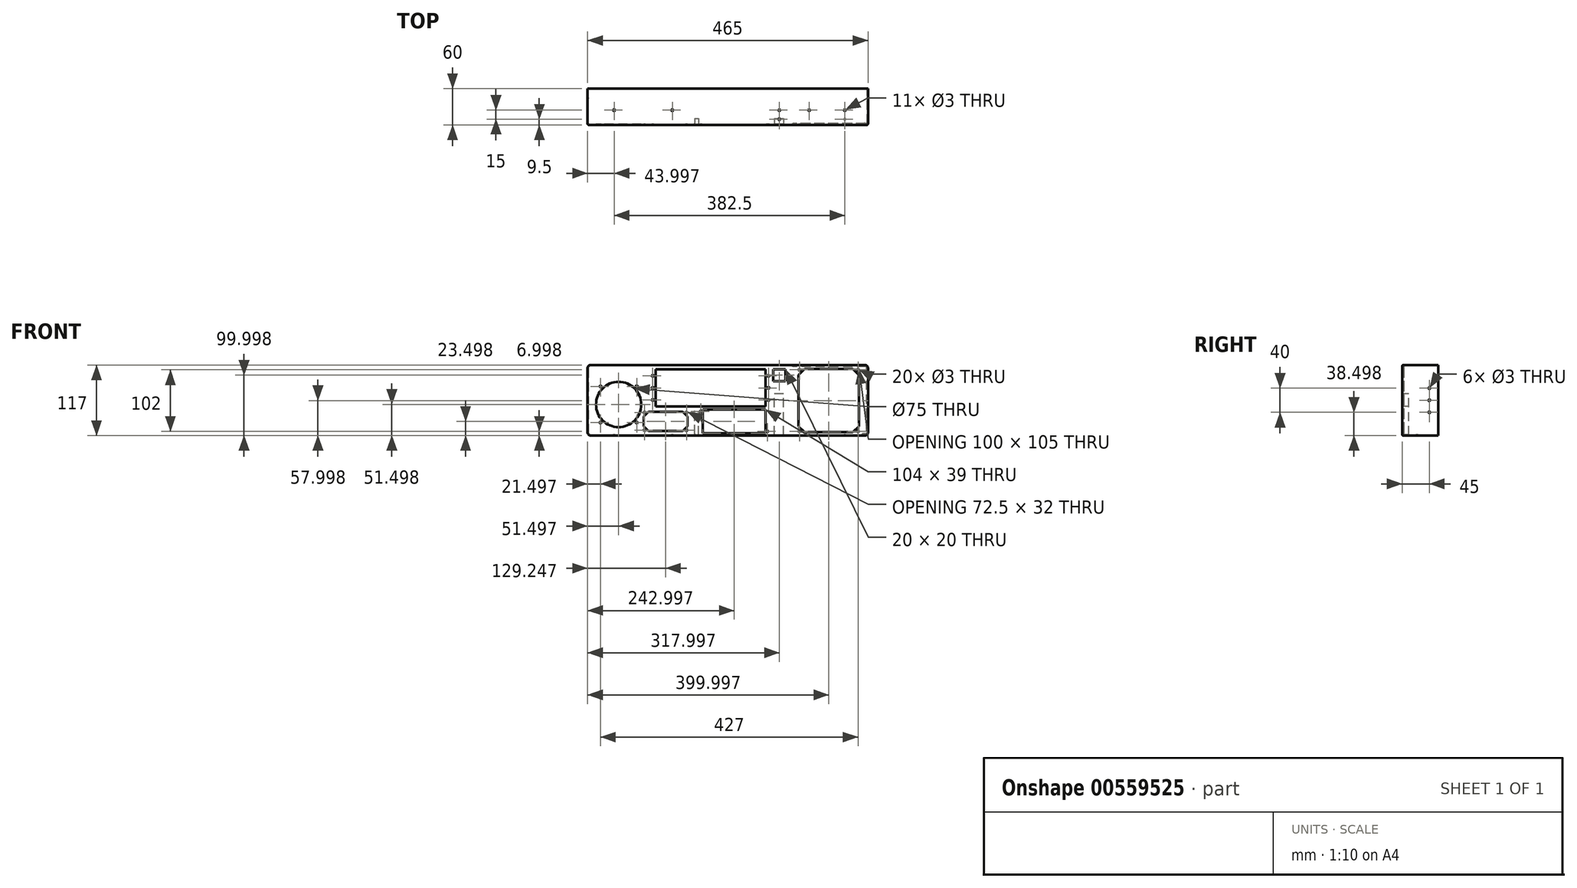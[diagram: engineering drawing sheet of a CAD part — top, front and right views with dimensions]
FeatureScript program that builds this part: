
annotation { "Feature Type Name" : "Feature", "Feature Type Description" : "" }
export const myFeature = defineFeature(function(context is Context, id is Id, definition is map)
    precondition{}
    {
        {
            var Q0;
            Q0=qCreatedBy(makeId("Front.planeOp"),FACE);
            var sketch = newSketch(context, id + "F0", { "sketchPlane" : qUnion([Q0])});
            skLineSegment(sketch, "E0.bottom", {"start": v(-245.15, 85.69) * mm, "end": v(219.85, 85.69) * mm});
            skLineSegment(sketch, "E0.top", {"start": v(-245.15, -31.31) * mm, "end": v(219.85, -31.31) * mm});
            skLineSegment(sketch, "E0.left", {"start": v(-245.15, 85.69) * mm, "end": v(-245.15, -31.31) * mm});
            skLineSegment(sketch, "E0.right", {"start": v(219.85, 85.69) * mm, "end": v(219.85, -31.31) * mm});
            skSolve(sketch);
        }
        {
            var Q0;
            Q0=qSketchRegion(id+"F0",true);
            var Q1;
            Q1=makeQuery(id+"F0.imprint","IMPRINT",FACE,{"disambiguationData":[TD([[makeQuery(id+"F0.imprint","IMPRINT",EDGE,{"derivedFrom":sQuery(id+"F0.wireOp",EDGE,"E0.bottom")}),-1.0]])]});
            extrude(context, id + "F1", {"entities" : qUnion([Q0, Q1]), "depth" : 60 * mm});
        }
        {
            var Q0;
            Q0=makeQuery(id+"F1.opExtrude","CAP_FACE",FACE,{"disambiguationData":[OSD([sQuery(id+"F0.wireOp",EDGE,"E0.bottom"),sQuery(id+"F0.wireOp",EDGE,"E0.top"),sQuery(id+"F0.wireOp",EDGE,"E0.left"),sQuery(id+"F0.wireOp",EDGE,"E0.right")])],"isStart":true});
            shell(context, id + "F2", {"entities" : qUnion([Q0]), "thickness" : 1 * mm});
        }
        {
            var Q0;
            Q0=makeQuery(id+"F1.opExtrude","CAP_FACE",FACE,{"disambiguationData":[OSD([sQuery(id+"F0.wireOp",EDGE,"E0.bottom"),sQuery(id+"F0.wireOp",EDGE,"E0.top"),sQuery(id+"F0.wireOp",EDGE,"E0.left"),sQuery(id+"F0.wireOp",EDGE,"E0.right")])],"isStart":false});
            var sketch = newSketch(context, id + "F3", { "sketchPlane" : qUnion([Q0])});
            skLineSegment(sketch, "E1.bottom", {"start": v(-132.15, 78.69) * mm, "end": v(49.85, 78.69) * mm});
            skLineSegment(sketch, "E1.top", {"start": v(-132.15, 16.69) * mm, "end": v(49.85, 16.69) * mm});
            skLineSegment(sketch, "E1.left", {"start": v(-132.15, 78.69) * mm, "end": v(-132.15, 16.69) * mm});
            skLineSegment(sketch, "E1.right", {"start": v(49.85, 78.69) * mm, "end": v(49.85, 16.69) * mm});
            skLineSegment(sketch, "E2.bottom", {"start": v(62.85, 78.69) * mm, "end": v(82.85, 78.69) * mm});
            skLineSegment(sketch, "E2.top", {"start": v(62.85, 58.69) * mm, "end": v(82.85, 58.69) * mm});
            skLineSegment(sketch, "E2.left", {"start": v(62.85, 78.69) * mm, "end": v(62.85, 58.69) * mm});
            skLineSegment(sketch, "E2.right", {"start": v(82.85, 78.69) * mm, "end": v(82.85, 58.69) * mm});
            skLineSegment(sketch, "E3.bottom", {"start": v(114.85, 79.19) * mm, "end": v(194.85, 79.19) * mm});
            skLineSegment(sketch, "E3.top", {"start": v(114.85, -25.81) * mm, "end": v(194.85, -25.81) * mm});
            skLineSegment(sketch, "E3.left", {"start": v(104.85, 69.19) * mm, "end": v(104.85, -15.81) * mm});
            skLineSegment(sketch, "E3.right", {"start": v(204.85, 69.19) * mm, "end": v(204.85, -15.81) * mm});
            skCircle(sketch, "E4", {"center": v(54.85, 67.69) * mm, "radius": 1.5 * mm});
            skCircle(sketch, "E5", {"center": v(54.85, 47.69) * mm, "radius": 1.5 * mm});
            skCircle(sketch, "E6", {"center": v(54.85, 27.69) * mm, "radius": 1.5 * mm});
            skCircle(sketch, "E7", {"center": v(106.35, 77.69) * mm, "radius": 1.5 * mm});
            skLineSegment(sketch, "E8", {"start": v(104.85, 69.19) * mm, "end": v(114.85, 79.19) * mm});
            skLineSegment(sketch, "E9.bottom", {"start": v(-144.65, 8.19) * mm, "end": v(-87.15, 8.19) * mm});
            skLineSegment(sketch, "E9.top", {"start": v(-144.65, -23.81) * mm, "end": v(-87.15, -23.81) * mm});
            skLineSegment(sketch, "E9.left", {"start": v(-152.15, 0.69) * mm, "end": v(-152.15, -16.31) * mm});
            skLineSegment(sketch, "E9.right", {"start": v(-79.65, 0.69) * mm, "end": v(-79.65, -16.31) * mm});
            skLineSegment(sketch, "E10", {"start": v(104.85, -15.81) * mm, "end": v(114.85, -25.81) * mm});
            skLineSegment(sketch, "E11", {"start": v(194.85, -25.81) * mm, "end": v(204.85, -15.81) * mm});
            skLineSegment(sketch, "E12", {"start": v(194.85, 79.19) * mm, "end": v(204.85, 69.19) * mm});
            skCircle(sketch, "E13", {"center": v(-193.65, 20.19) * mm, "radius": 37.5 * mm});
            skLineSegment(sketch, "E14", {"start": v(-152.15, 0.69) * mm, "end": v(-144.65, 8.19) * mm});
            skLineSegment(sketch, "E15", {"start": v(-87.15, 8.19) * mm, "end": v(-79.65, 0.69) * mm});
            skLineSegment(sketch, "E16", {"start": v(-79.65, -16.31) * mm, "end": v(-87.15, -23.81) * mm});
            skLineSegment(sketch, "E17", {"start": v(-152.15, -16.31) * mm, "end": v(-144.65, -23.81) * mm});
            skCircle(sketch, "E18", {"center": v(-137.15, 67.69) * mm, "radius": 1.5 * mm});
            skCircle(sketch, "E19", {"center": v(-137.15, 47.69) * mm, "radius": 1.5 * mm});
            skCircle(sketch, "E20", {"center": v(-137.15, 27.69) * mm, "radius": 1.5 * mm});
            skCircle(sketch, "E21", {"center": v(-223.65, 50.19) * mm, "radius": 1.5 * mm});
            skCircle(sketch, "E22", {"center": v(-223.65, -9.81) * mm, "radius": 1.5 * mm});
            skCircle(sketch, "E23", {"center": v(-163.65, -9.81) * mm, "radius": 1.5 * mm});
            skCircle(sketch, "E24", {"center": v(-163.65, 50.19) * mm, "radius": 1.5 * mm});
            skCircle(sketch, "E25", {"center": v(-57.15, 8.69) * mm, "radius": 1.5 * mm});
            skCircle(sketch, "E26", {"center": v(52.85, -24.31) * mm, "radius": 1.5 * mm});
            skLineSegment(sketch, "E27.bottom", {"start": v(-54.15, 11.69) * mm, "end": v(49.85, 11.69) * mm});
            skLineSegment(sketch, "E27.top", {"start": v(-54.15, -27.31) * mm, "end": v(49.85, -27.31) * mm});
            skLineSegment(sketch, "E27.left", {"start": v(-54.15, 11.69) * mm, "end": v(-54.15, -27.31) * mm});
            skLineSegment(sketch, "E27.right", {"start": v(49.85, 11.69) * mm, "end": v(49.85, -27.31) * mm});
            skLineSegment(sketch, "E28.bottom", {"start": v(-163.65, -9.81) * mm, "end": v(-223.65, -9.81) * mm, "construction": true});
            skLineSegment(sketch, "E28.top", {"start": v(-163.65, 50.19) * mm, "end": v(-223.65, 50.19) * mm, "construction": true});
            skLineSegment(sketch, "E28.left", {"start": v(-163.65, -9.81) * mm, "end": v(-163.65, 50.19) * mm, "construction": true});
            skLineSegment(sketch, "E28.right", {"start": v(-223.65, -9.81) * mm, "end": v(-223.65, 50.19) * mm, "construction": true});
            skCircle(sketch, "E29", {"center": v(-150.65, 6.69) * mm, "radius": 1.5 * mm});
            skCircle(sketch, "E30", {"center": v(-81.15, 6.69) * mm, "radius": 1.5 * mm});
            skCircle(sketch, "E31", {"center": v(-150.65, -22.31) * mm, "radius": 1.5 * mm});
            skCircle(sketch, "E32", {"center": v(-81.15, -22.31) * mm, "radius": 1.5 * mm});
            skCircle(sketch, "E33", {"center": v(203.35, 77.69) * mm, "radius": 1.5 * mm});
            skCircle(sketch, "E34", {"center": v(106.35, -24.31) * mm, "radius": 1.5 * mm});
            skCircle(sketch, "E35", {"center": v(203.35, -24.31) * mm, "radius": 1.5 * mm});
            skSolve(sketch);
        }
        {
            var Q0;
            Q0=qSketchRegion(id+"F3",true);
            extrude(context, id + "F4", {"entities" : qUnion([Q0]), "operationType" : NewBodyOperationType.REMOVE, "oppositeDirection" : true, "depth" : 25 * mm});
        }
        {
            var Q0;
            Q0=makeQuery(id+"F1.opExtrude","SWEPT_FACE",FACE,{"disambiguationData":[OSD([sQuery(id+"F0.wireOp",EDGE,"E0.left")])]});
            var sketch = newSketch(context, id + "F5", { "sketchPlane" : qUnion([Q0])});
            skCircle(sketch, "E36", {"center": v(15, 47.19) * mm, "radius": 1.5 * mm});
            skCircle(sketch, "E37", {"center": v(15, 7.19) * mm, "radius": 1.5 * mm});
            skLineSegment(sketch, "E38", {"start": v(-16.01, 27.19) * mm, "end": v(37.35, 27.19) * mm, "construction": true});
            skPoint(sketch, "E39.middle.positionSnap0", {"position": v(0, 27.19) * mm});
            skPoint(sketch, "E39.centerSnap0", {"position": v(0, 27.19) * mm});
            skCircle(sketch, "E40", {"center": v(15, 27.19) * mm, "radius": 1.5 * mm});
            skSolve(sketch);
        }
        {
            var Q0;
            Q0=qSketchRegion(id+"F5",true);
            extrude(context, id + "F6", {"entities" : qUnion([Q0]), "operationType" : NewBodyOperationType.REMOVE, "oppositeDirection" : true, "depth" : 500 * mm});
        }
        {
            var Q0;
            Q0=makeQuery(id+"F1.opExtrude","SWEPT_FACE",FACE,{"disambiguationData":[OSD([sQuery(id+"F0.wireOp",EDGE,"E0.bottom")])]});
            var sketch = newSketch(context, id + "F7", { "sketchPlane" : qUnion([Q0])});
            skCircle(sketch, "E41", {"center": v(-201.15, -35.5) * mm, "radius": 1.5 * mm});
            skCircle(sketch, "E42", {"center": v(-104.65, -35.5) * mm, "radius": 1.5 * mm});
            skCircle(sketch, "E43", {"center": v(122.35, -35.5) * mm, "radius": 1.5 * mm});
            skCircle(sketch, "E44", {"center": v(181.35, -35.5) * mm, "radius": 1.5 * mm});
            skCircle(sketch, "E45", {"center": v(72.85, -35.5) * mm, "radius": 1.5 * mm});
            skCircle(sketch, "E46", {"center": v(72.85, -50.5) * mm, "radius": 1.5 * mm});
            skCircle(sketch, "E47", {"center": v(181.35, -50.5) * mm, "radius": 1.5 * mm, "construction": true});
            skSolve(sketch);
        }
        {
            var Q0;
            Q0=makeQuery(id+"F7.imprint","IMPRINT",FACE,{"disambiguationData":[TD([[makeQuery(id+"F7.imprint","IMPRINT",EDGE,{"derivedFrom":sQuery(id+"F7.wireOp",EDGE,"E41")}),1.0]])]});
            var Q1;
            Q1=makeQuery(id+"F7.imprint","IMPRINT",FACE,{"disambiguationData":[TD([[makeQuery(id+"F7.imprint","IMPRINT",EDGE,{"derivedFrom":sQuery(id+"F7.wireOp",EDGE,"E42")}),1.0]])]});
            var Q2;
            Q2=makeQuery(id+"F7.imprint","IMPRINT",FACE,{"disambiguationData":[TD([[makeQuery(id+"F7.imprint","IMPRINT",EDGE,{"derivedFrom":sQuery(id+"F7.wireOp",EDGE,"E43")}),1.0]])]});
            var Q3;
            Q3=makeQuery(id+"F7.imprint","IMPRINT",FACE,{"disambiguationData":[TD([[makeQuery(id+"F7.imprint","IMPRINT",EDGE,{"derivedFrom":sQuery(id+"F7.wireOp",EDGE,"E44")}),1.0]])]});
            var Q4;
            Q4=makeQuery(id+"F7.imprint","IMPRINT",FACE,{"disambiguationData":[TD([[makeQuery(id+"F7.imprint","IMPRINT",EDGE,{"derivedFrom":sQuery(id+"F7.wireOp",EDGE,"E47")}),1.0]])]});
            extrude(context, id + "F8", {"entities" : qUnion([Q0, Q1, Q2, Q3, Q4]), "operationType" : NewBodyOperationType.REMOVE, "endBound" : BoundingType.THROUGH_ALL, "oppositeDirection" : true, "depth" : 117 * mm});
        }
        {
            var Q0;
            Q0=makeQuery(id+"F7.imprint","IMPRINT",FACE,{"disambiguationData":[TD([[makeQuery(id+"F7.imprint","IMPRINT",EDGE,{"derivedFrom":sQuery(id+"F7.wireOp",EDGE,"E45")}),1.0]])]});
            var Q1;
            Q1=makeQuery(id+"F7.imprint","IMPRINT",FACE,{"disambiguationData":[TD([[makeQuery(id+"F7.imprint","IMPRINT",EDGE,{"derivedFrom":sQuery(id+"F7.wireOp",EDGE,"E46")}),1.0]])]});
            extrude(context, id + "F9", {"entities" : qUnion([Q0, Q1]), "operationType" : NewBodyOperationType.REMOVE, "oppositeDirection" : true, "depth" : 2 * mm});
        }
        {
            var Q0;
            Q0=makeQuery(id+"F1.opExtrude","SWEPT_FACE",FACE,{"disambiguationData":[OSD([sQuery(id+"F0.wireOp",EDGE,"E0.top")])]});
            var sketch = newSketch(context, id + "F10", { "sketchPlane" : qUnion([Q0])});
            skCircle(sketch, "E48", {"center": v(181.35, 50.5) * mm, "radius": 1.5 * mm});
            skCircle(sketch, "E49.0", {"center": v(181.35, 35.5) * mm, "radius": 1.5 * mm, "construction": true});
            skSolve(sketch);
        }
        {
            var Q0;
            Q0=qSketchRegion(id+"F10",true);
            extrude(context, id + "F11", {"entities" : qUnion([Q0]), "operationType" : NewBodyOperationType.REMOVE, "oppositeDirection" : true, "depth" : 2 * mm});
        }
        {
            var Q0;
            Q0=makeQuery(id+"F2.opShell","OFFSET_FACE",FACE,{"disambiguationData":[OSD([sQuery(id+"F0.wireOp",EDGE,"E0.bottom"),sQuery(id+"F0.wireOp",EDGE,"E0.top"),sQuery(id+"F0.wireOp",EDGE,"E0.left"),sQuery(id+"F0.wireOp",EDGE,"E0.right")])]});
            var sketch = newSketch(context, id + "F12", { "sketchPlane" : qUnion([Q0])});
            skLineSegment(sketch, "E50.bottom", {"start": v(-79.86, -30.31) * mm, "end": v(-64.86, -30.31) * mm});
            skLineSegment(sketch, "E50.top", {"start": v(-79.86, 38.12) * mm, "end": v(-64.86, 38.12) * mm});
            skLineSegment(sketch, "E50.left", {"start": v(-79.86, -30.31) * mm, "end": v(-79.86, 38.12) * mm});
            skLineSegment(sketch, "E50.right", {"start": v(-64.86, -30.31) * mm, "end": v(-64.86, 38.12) * mm});
            skLineSegment(sketch, "E51.bottom", {"start": v(61.44, -30.31) * mm, "end": v(67.44, -30.31) * mm});
            skLineSegment(sketch, "E51.top", {"start": v(61.44, 16.69) * mm, "end": v(67.44, 16.69) * mm});
            skLineSegment(sketch, "E51.left", {"start": v(61.44, -30.31) * mm, "end": v(61.44, 16.69) * mm});
            skLineSegment(sketch, "E51.right", {"start": v(67.44, -30.31) * mm, "end": v(67.44, 16.69) * mm});
            skLineSegment(sketch, "E52.bottom", {"start": v(-64.86, 16.19) * mm, "end": v(61.44, 16.19) * mm});
            skLineSegment(sketch, "E52.top", {"start": v(-64.86, 12.19) * mm, "end": v(61.44, 12.19) * mm});
            skLineSegment(sketch, "E52.left", {"start": v(-64.86, 16.19) * mm, "end": v(-64.86, 12.19) * mm});
            skLineSegment(sketch, "E52.right", {"start": v(61.44, 16.19) * mm, "end": v(61.44, 12.19) * mm});
            skLineSegment(sketch, "E53.bottom", {"start": v(-55.88, 84.69) * mm, "end": v(244.15, 84.69) * mm});
            skLineSegment(sketch, "E53.top", {"start": v(-55.88, 81.41) * mm, "end": v(244.15, 81.41) * mm});
            skLineSegment(sketch, "E53.left", {"start": v(-55.88, 84.69) * mm, "end": v(-55.88, 81.41) * mm});
            skLineSegment(sketch, "E53.right", {"start": v(244.15, 84.69) * mm, "end": v(244.15, 81.41) * mm});
            skLineSegment(sketch, "E54.bottom", {"start": v(244.15, 81.41) * mm, "end": v(239.22, 81.41) * mm});
            skLineSegment(sketch, "E54.top", {"start": v(244.15, -30.31) * mm, "end": v(239.22, -30.31) * mm});
            skLineSegment(sketch, "E54.left", {"start": v(244.15, 81.41) * mm, "end": v(244.15, -30.31) * mm});
            skLineSegment(sketch, "E54.right", {"start": v(239.22, 81.41) * mm, "end": v(239.22, -30.31) * mm});
            skLineSegment(sketch, "E55.bottom", {"start": v(-218.85, 84.69) * mm, "end": v(-216.85, 84.69) * mm});
            skLineSegment(sketch, "E55.top", {"start": v(-218.85, -30.31) * mm, "end": v(-216.85, -30.31) * mm});
            skLineSegment(sketch, "E55.left", {"start": v(-218.85, 84.69) * mm, "end": v(-218.85, -30.31) * mm});
            skLineSegment(sketch, "E55.right", {"start": v(-216.85, 84.69) * mm, "end": v(-216.85, -30.31) * mm});
            skLineSegment(sketch, "E56.bottom", {"start": v(-216.85, -30.31) * mm, "end": v(-210.85, -30.31) * mm});
            skLineSegment(sketch, "E56.top", {"start": v(-216.85, -28.31) * mm, "end": v(-210.85, -28.31) * mm});
            skLineSegment(sketch, "E56.left", {"start": v(-216.85, -30.31) * mm, "end": v(-216.85, -28.31) * mm});
            skLineSegment(sketch, "E56.right", {"start": v(-210.85, -30.31) * mm, "end": v(-210.85, -28.31) * mm});
            skLineSegment(sketch, "E57.bottom", {"start": v(-216.85, 84.69) * mm, "end": v(-94.85, 84.69) * mm});
            skLineSegment(sketch, "E57.top", {"start": v(-216.85, 82.69) * mm, "end": v(-94.85, 82.69) * mm});
            skLineSegment(sketch, "E57.left", {"start": v(-216.85, 84.69) * mm, "end": v(-216.85, 82.69) * mm});
            skLineSegment(sketch, "E57.right", {"start": v(-94.85, 84.69) * mm, "end": v(-94.85, 82.69) * mm});
            skLineSegment(sketch, "E58.bottom", {"start": v(-94.85, 82.69) * mm, "end": v(-96.85, 82.69) * mm});
            skLineSegment(sketch, "E58.top", {"start": v(-94.85, -30.31) * mm, "end": v(-96.85, -30.31) * mm});
            skLineSegment(sketch, "E58.left", {"start": v(-94.85, 82.69) * mm, "end": v(-94.85, -30.31) * mm});
            skLineSegment(sketch, "E58.right", {"start": v(-96.85, 82.69) * mm, "end": v(-96.85, -30.31) * mm});
            skSolve(sketch);
        }
        {
            var Q0;
            {var subQ1=sQuery(id+"F12.wireOp",EDGE,"E50.bottom");Q0=makeQuery(id+"F12.imprint","IMPRINT",FACE,{"disambiguationData":[TD([[makeQuery(id+"F12.imprint","IMPRINT",EDGE,{"derivedFrom":subQ1}),-1.0]])]});}
            var Q1;
            {var subQ4=sQuery(id+"F12.wireOp",EDGE,"E51.bottom");Q1=makeQuery(id+"F12.imprint","IMPRINT",FACE,{"disambiguationData":[TD([[makeQuery(id+"F12.imprint","IMPRINT",EDGE,{"derivedFrom":subQ4}),-1.0]])]});}
            extrude(context, id + "F13", {"entities" : qUnion([Q0, Q1]), "operationType" : NewBodyOperationType.ADD, "depth" : 10 * mm});
        }
        {
            var Q0;
            Q0=makeQuery(id+"F12.imprint","IMPRINT",FACE,{"disambiguationData":[TD([[makeQuery(id+"F12.imprint","IMPRINT",EDGE,{"derivedFrom":sQuery(id+"F12.wireOp",EDGE,"E55.bottom")}),1.0]])]});
            var Q1;
            Q1=makeQuery(id+"F12.imprint","IMPRINT",FACE,{"disambiguationData":[TD([[makeQuery(id+"F12.imprint","IMPRINT",EDGE,{"derivedFrom":sQuery(id+"F12.wireOp",EDGE,"E56.bottom")}),-1.0]])]});
            var Q2;
            Q2=makeQuery(id+"F12.imprint","IMPRINT",FACE,{"disambiguationData":[TD([[makeQuery(id+"F12.imprint","IMPRINT",EDGE,{"derivedFrom":sQuery(id+"F12.wireOp",EDGE,"E57.bottom")}),1.0]])]});
            extrude(context, id + "F14", {"entities" : qUnion([Q0, Q1, Q2]), "operationType" : NewBodyOperationType.ADD, "depth" : 1.5 * mm});
        }
        {
            var Q0;
            Q0=makeQuery(id+"F1.opExtrude","SWEPT_EDGE",EDGE,{"disambiguationData":[OSD([sQuery(id+"F0.wireOp",EDGE,"E0.bottom"),sQuery(id+"F0.wireOp",EDGE,"E0.left")])]});
            var Q1;
            Q1=makeQuery(id+"F1.opExtrude","SWEPT_EDGE",EDGE,{"disambiguationData":[OSD([sQuery(id+"F0.wireOp",EDGE,"E0.bottom"),sQuery(id+"F0.wireOp",EDGE,"E0.right")])]});
            var Q2;
            Q2=makeQuery(id+"F1.opExtrude","SWEPT_EDGE",EDGE,{"disambiguationData":[OSD([sQuery(id+"F0.wireOp",EDGE,"E0.top"),sQuery(id+"F0.wireOp",EDGE,"E0.right")])]});
            var Q3;
            Q3=makeQuery(id+"F1.opExtrude","SWEPT_EDGE",EDGE,{"disambiguationData":[OSD([sQuery(id+"F0.wireOp",EDGE,"E0.top"),sQuery(id+"F0.wireOp",EDGE,"E0.left")])]});
            var Q4;
            Q4=makeQuery(id+"F2.opShell","OFFSET_EDGE",EDGE,{"disambiguationData":[OSD([sQuery(id+"F0.wireOp",EDGE,"E0.bottom"),sQuery(id+"F0.wireOp",EDGE,"E0.left")])]});
            var Q5;
            Q5=makeQuery(id+"F2.opShell","OFFSET_EDGE",EDGE,{"disambiguationData":[OSD([sQuery(id+"F0.wireOp",EDGE,"E0.top"),sQuery(id+"F0.wireOp",EDGE,"E0.left")])]});
            var Q6;
            Q6=makeQuery(id+"F2.opShell","OFFSET_EDGE",EDGE,{"disambiguationData":[OSD([sQuery(id+"F0.wireOp",EDGE,"E0.top"),sQuery(id+"F0.wireOp",EDGE,"E0.right")])]});
            var Q7;
            Q7=makeQuery(id+"F2.opShell","OFFSET_EDGE",EDGE,{"disambiguationData":[OSD([sQuery(id+"F0.wireOp",EDGE,"E0.bottom"),sQuery(id+"F0.wireOp",EDGE,"E0.right")])]});
            fillet(context, id + "F15", {"entities" : qUnion([Q0, Q1, Q2, Q3, Q4, Q5, Q6, Q7]), "radius" : 5 * mm, "tangentPropagation" : true, "allowEdgeOverflow" : false});
        }
        {
            var Q0;
            {var subQ0=sQuery(id+"F0.wireOp",EDGE,"E0.right");var subQ1=sQuery(id+"F0.wireOp",EDGE,"E0.bottom");Q0=makeQuery(id+"F15.opFillet","BLEND_EDGE",EDGE,{"blendedFrom":[makeQuery(id+"F1.opExtrude","SWEPT_EDGE",EDGE,{"disambiguationData":[OSD([subQ1,subQ0])]}),makeQuery(id+"F1.opExtrude","CAP_FACE",FACE,{"disambiguationData":[OSD([subQ1,sQuery(id+"F0.wireOp",EDGE,"E0.top"),sQuery(id+"F0.wireOp",EDGE,"E0.left"),subQ0])],"isStart":false})],"blendedInto":[makeQuery(id+"F1.opExtrude","CAP_FACE",FACE,{"disambiguationData":[OSD([subQ1,sQuery(id+"F0.wireOp",EDGE,"E0.top"),sQuery(id+"F0.wireOp",EDGE,"E0.left"),subQ0])],"isStart":false})]});}
            var Q1;
            {var subQ0=sQuery(id+"F0.wireOp",EDGE,"E0.bottom");Q1=makeQuery(id+"F2.opShell","OFFSET_EDGE",EDGE,{"disambiguationData":[OSD([subQ0]),TDD([makeQuery(id+"F1.opExtrude","CAP_EDGE",EDGE,{"disambiguationData":[OSD([subQ0])],"isStart":false})])]});}
            fillet(context, id + "F16", {"entities" : qUnion([Q0, Q1]), "radius" : 2 * mm, "tangentPropagation" : true, "allowEdgeOverflow" : false});
        }
    });
